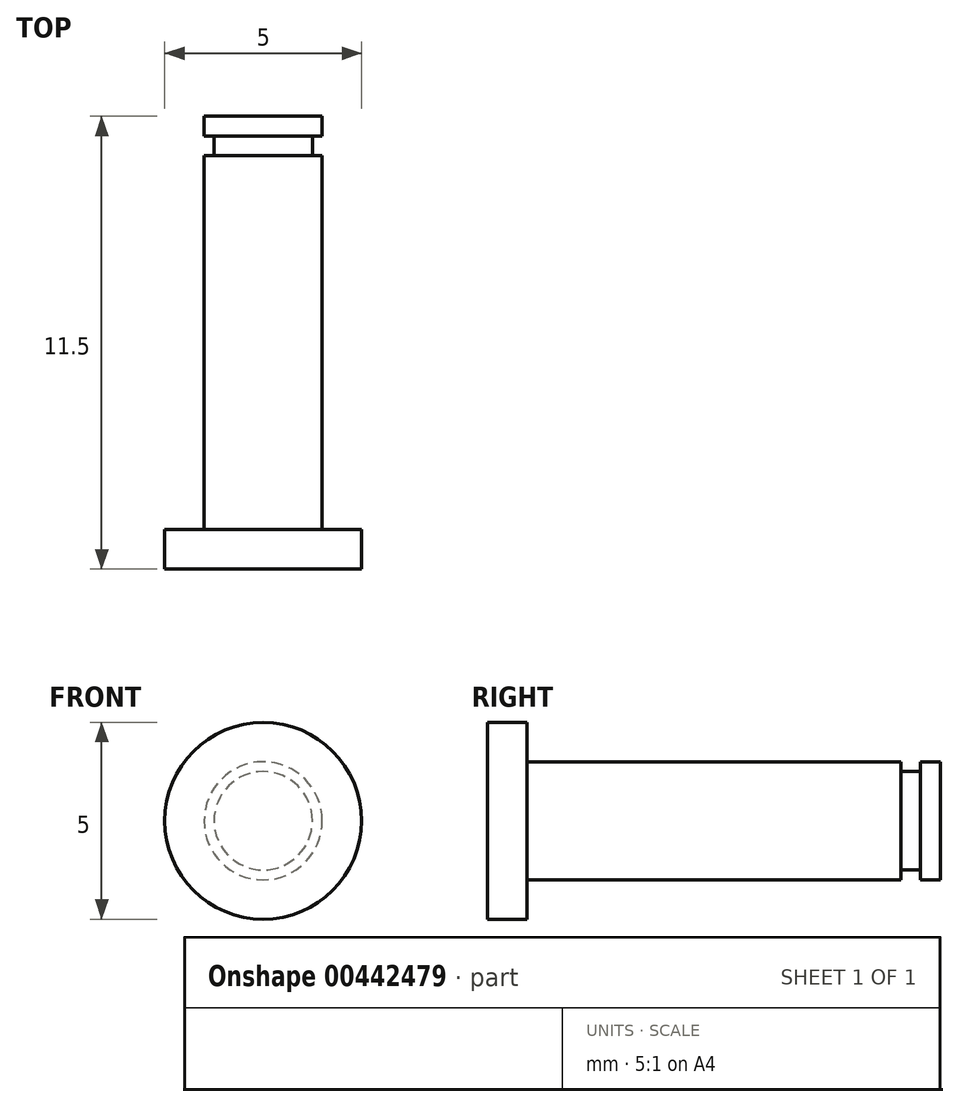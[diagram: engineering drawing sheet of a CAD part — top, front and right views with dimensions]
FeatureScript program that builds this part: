
annotation { "Feature Type Name" : "Feature", "Feature Type Description" : "" }
export const myFeature = defineFeature(function(context is Context, id is Id, definition is map)
    precondition{}
    {
        {
            var Q0;
            Q0=qCreatedBy(makeId("Front.planeOp"),FACE);
            var sketch = newSketch(context, id + "F0", { "sketchPlane" : qUnion([Q0])});
            skCircle(sketch, "E0", {"center": v(0, 0) * mm, "radius": 1.5 * mm});
            skSolve(sketch);
        }
        {
            var Q0;
            Q0=qSketchRegion(id+"F0",true);
            extrude(context, id + "F1", {"entities" : qUnion([Q0]), "depth" : 9.5 * mm});
        }
        {
            var Q0;
            Q0=makeQuery(id+"F1.opExtrude","CAP_FACE",FACE,{"disambiguationData":[OSD([sQuery(id+"F0.wireOp",EDGE,"E0")])],"isStart":false});
            var sketch = newSketch(context, id + "F2", { "sketchPlane" : qUnion([Q0])});
            skCircle(sketch, "E1", {"center": v(0, 0) * mm, "radius": 2.5 * mm});
            skSolve(sketch);
        }
        {
            var Q0;
            Q0=qSketchRegion(id+"F2",true);
            extrude(context, id + "F3", {"entities" : qUnion([Q0]), "operationType" : NewBodyOperationType.ADD, "depth" : 1 * mm});
        }
        {
            var Q0;
            Q0=makeQuery(id+"F1.opExtrude","CAP_FACE",FACE,{"disambiguationData":[OSD([sQuery(id+"F0.wireOp",EDGE,"E0")])],"isStart":true});
            var sketch = newSketch(context, id + "F4", { "sketchPlane" : qUnion([Q0])});
            skCircle(sketch, "E2", {"center": v(0, 0) * mm, "radius": 1.25 * mm});
            skSolve(sketch);
        }
        {
            var Q0;
            Q0 = qSketchRegion(id + "F4", true);
            extrude(context, id + "F5", {"entities" : qUnion([Q0]), "operationType" : NewBodyOperationType.ADD, "depth" : .5 * mm});
        }
        {
            var Q0;
            Q0=makeQuery(id+"F5.opExtrude","CAP_FACE",FACE,{"disambiguationData":[OSD([sQuery(id+"F4.wireOp",EDGE,"E2")])],"isStart":false});
            var sketch = newSketch(context, id + "F6", { "sketchPlane" : qUnion([Q0])});
            skCircle(sketch, "E3", {"center": v(0, 0) * mm, "radius": 1.5 * mm});
            skSolve(sketch);
        }
        {
            var Q0;
            Q0 = qSketchRegion(id + "F6", true);
            extrude(context, id + "F7", {"entities" : qUnion([Q0]), "operationType" : NewBodyOperationType.ADD, "depth" : .5 * mm});
        }
    });
